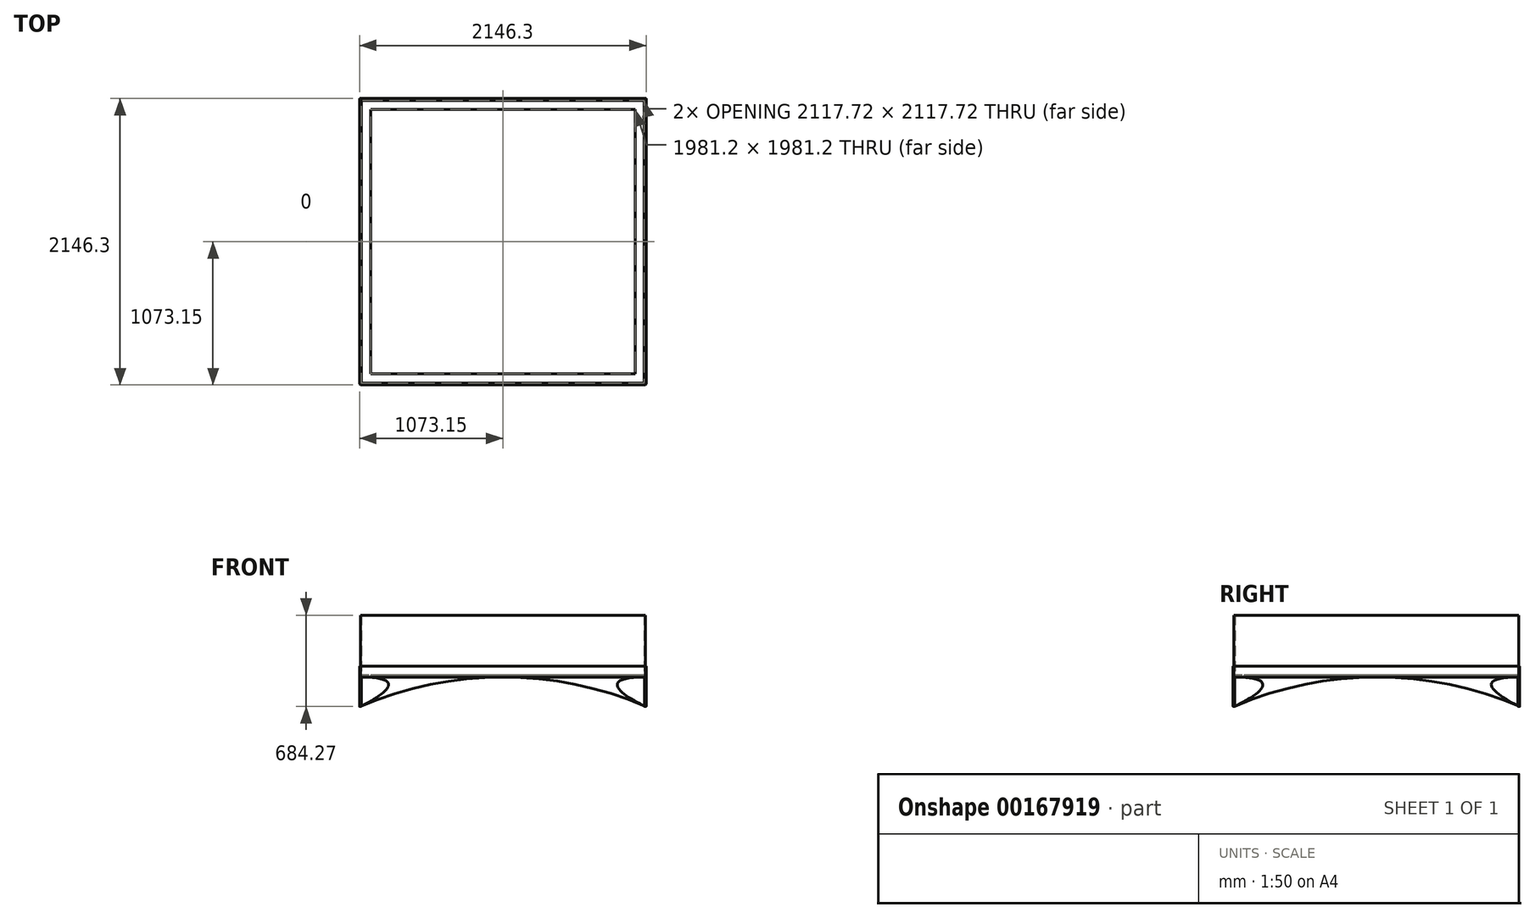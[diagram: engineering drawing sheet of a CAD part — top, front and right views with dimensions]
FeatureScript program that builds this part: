
annotation { "Feature Type Name" : "Feature", "Feature Type Description" : "" }
export const myFeature = defineFeature(function(context is Context, id is Id, definition is map)
    precondition{}
    {
        {
            var Q0;
            Q0=qCreatedBy(makeId("Top.planeOp"),FACE);
            var sketch = newSketch(context, id + "F0", { "sketchPlane" : qUnion([Q0])});
            skLineSegment(sketch, "E0.bottom", {"start": v(1066.8, 1066.8) * mm, "end": v(-1060.45, 1066.8) * mm});
            skLineSegment(sketch, "E0.top", {"start": v(1066.8, -1066.8) * mm, "end": v(-1066.8, -1066.8) * mm});
            skLineSegment(sketch, "E0.left", {"start": v(1066.8, 1066.8) * mm, "end": v(1066.8, -1066.8) * mm});
            skLineSegment(sketch, "E0.right", {"start": v(-1066.8, 1060.45) * mm, "end": v(-1066.8, -1066.8) * mm});
            skPoint(sketch, "E0.middle", {"position": v(0, 0) * mm});
            skLineSegment(sketch, "E1", {"start": v(-1073.15, 1066.8) * mm, "end": v(-1073.15, -1066.8) * mm});
            skLineSegment(sketch, "E2", {"start": v(-1066.8, 1073.15) * mm, "end": v(1066.8, 1073.15) * mm});
            skLineSegment(sketch, "E3", {"start": v(-1066.8, 1073.15) * mm, "end": v(-1073.15, 1066.8) * mm});
            skLineSegment(sketch, "E4.MirrorCS", {"start": v(1073.15, 1066.8) * mm, "end": v(1073.15, -1066.8) * mm});
            skLineSegment(sketch, "E5.MirrorCS", {"start": v(1066.8, 1073.15) * mm, "end": v(1073.15, 1066.8) * mm});
            skLineSegment(sketch, "E6.MirrorCS", {"start": v(-1066.8, -1073.15) * mm, "end": v(1066.8, -1073.15) * mm});
            skLineSegment(sketch, "E7.MirrorCS", {"start": v(1066.8, -1073.15) * mm, "end": v(1073.15, -1066.8) * mm});
            skLineSegment(sketch, "E8.MirrorCS", {"start": v(1066.8, -1066.8) * mm, "end": v(1066.8, 1066.8) * mm});
            skLineSegment(sketch, "E9.MirrorCS", {"start": v(1073.15, -1066.8) * mm, "end": v(1073.15, 1066.8) * mm});
            skLineSegment(sketch, "E10.MirrorCS", {"start": v(-1066.8, -1073.15) * mm, "end": v(-1073.15, -1066.8) * mm});
            skLineSegment(sketch, "E11.bottom", {"start": v(990.6, 990.6) * mm, "end": v(-990.6, 990.6) * mm});
            skLineSegment(sketch, "E11.top", {"start": v(990.6, -990.6) * mm, "end": v(-990.6, -990.6) * mm});
            skLineSegment(sketch, "E11.left", {"start": v(990.6, 990.6) * mm, "end": v(990.6, -990.6) * mm});
            skLineSegment(sketch, "E11.right", {"start": v(-990.6, 990.6) * mm, "end": v(-990.6, -990.6) * mm});
            skLineSegment(sketch, "E12.bottom", {"start": v(1052.51, 1058.86) * mm, "end": v(-1052.51, 1058.86) * mm});
            skLineSegment(sketch, "E12.top", {"start": v(1058.86, -1058.86) * mm, "end": v(-1058.86, -1058.86) * mm});
            skLineSegment(sketch, "E12.left", {"start": v(1058.86, 1052.51) * mm, "end": v(1058.86, -1058.86) * mm});
            skLineSegment(sketch, "E12.right", {"start": v(-1058.86, 1052.51) * mm, "end": v(-1058.86, -1058.86) * mm});
            skPoint(sketch, "E13.visualSharp", {"position": v(-1058.86, 1058.86) * mm});
            skArc(sketch, "E13.filletArc", {"start": v(-1052.51, 1058.86) * mm, "mid": v(-1057, 1057) * mm, "end": v(-1058.86, 1052.51) * mm});
            skPoint(sketch, "E14.visualSharp", {"position": v(-1066.8, 1066.8) * mm});
            skArc(sketch, "E14.filletArc", {"start": v(-1060.45, 1066.8) * mm, "mid": v(-1064.94, 1064.94) * mm, "end": v(-1066.8, 1060.45) * mm});
            skPoint(sketch, "E15.visualSharp", {"position": v(1058.86, 1058.86) * mm});
            skArc(sketch, "E15.filletArc", {"start": v(1058.86, 1052.51) * mm, "mid": v(1057, 1057) * mm, "end": v(1052.51, 1058.86) * mm});
            skSolve(sketch);
        }
        {
            var Q0;
            Q0 = qSketchRegion(id + "F0", true);
            extrude(context, id + "F1", {"entities" : qUnion([Q0]), "depth" : 76.2 * mm, "hasSecondDirection" : true, "secondDirectionOppositeDirection" : true, "secondDirectionDepth" : 6.35 * mm});
        }
        {
            var Q0;
            Q0=makeQuery(id+"F0.imprint","IMPRINT",FACE,{"disambiguationData":[TD([[makeQuery(id+"F0.imprint","IMPRINT",EDGE,{"derivedFrom":sQuery(id+"F0.wireOp",EDGE,"E0.bottom")}),1.0]])]});
            var Q1;
            Q1=makeQuery(id+"F0.imprint","IMPRINT",FACE,{"disambiguationData":[TD([[makeQuery(id+"F0.imprint","IMPRINT",EDGE,{"derivedFrom":sQuery(id+"F0.wireOp",EDGE,"E11.bottom")}),-1.0]])]});
            extrude(context, id + "F2", {"entities" : qUnion([Q0, Q1]), "operationType" : NewBodyOperationType.ADD, "oppositeDirection" : true, "depth" : 6.35 * mm});
        }
        {
            var Q0;
            Q0=makeQuery(id+"F0.imprint","IMPRINT",FACE,{"disambiguationData":[TD([[makeQuery(id+"F0.imprint","IMPRINT",EDGE,{"derivedFrom":sQuery(id+"F0.wireOp",EDGE,"E11.bottom")}),1.0]])]});
            var Q1;
            Q1=makeQuery(id+"F0.imprint","IMPRINT",FACE,{"disambiguationData":[TD([[makeQuery(id+"F0.imprint","IMPRINT",EDGE,{"derivedFrom":sQuery(id+"F0.wireOp",EDGE,"E0.bottom")}),1.0]])]});
            extrude(context, id + "F3", {"entities" : qUnion([Q0, Q1]), "depth" : 9.52 * mm});
        }
        {
            var Q0;
            Q0=makeQuery(id+"F0.imprint","IMPRINT",FACE,{"disambiguationData":[TD([[makeQuery(id+"F0.imprint","IMPRINT",EDGE,{"derivedFrom":sQuery(id+"F0.wireOp",EDGE,"E0.bottom")}),1.0]])]});
            extrude(context, id + "F4", {"entities" : qUnion([Q0]), "depth" : 457.2 * mm});
        }
        {
            var Q0;
            Q0=makeQuery(id+"F1.opExtrude","SWEPT_FACE",FACE,{"disambiguationData":[OSD([sQuery(id+"F0.wireOp",EDGE,"E6.MirrorCS")])]});
            var sketch = newSketch(context, id + "F5", { "sketchPlane" : qUnion([Q0])});
            skArc(sketch, "E16", {"start": v(1066.8, -224.76) * mm, "mid": v(-0.24, -6.61) * mm, "end": v(-1066.8, -227.07) * mm});
            skPoint(sketch, "E16.endSnap0", {"position": v(-1066.8, 34.93) * mm});
            skFitSpline(sketch, "E17", {"points": [v(-1066.8, -6.35) * mm, v(-1066.8, -227.07) * mm], "startDerivative": vector(1189.41, 0) * mm, "endDerivative": vector(-424.25, -208.28) * mm});
            skFitSpline(sketch, "E18", {"points": [v(1066.8, -6.35) * mm, v(1066.8, -224.76) * mm], "startDerivative": vector(-1161.94, 0) * mm, "endDerivative": vector(443.87, -209.2) * mm});
            skSolve(sketch);
        }
        {
            var Q0;
            Q0=makeQuery(id+"F5.imprint","IMPRINT",FACE,{"disambiguationData":[TD([[makeQuery(id+"F5.imprint","IMPRINT",EDGE,{"derivedFrom":sQuery(id+"F5.wireOp",EDGE,"E16")}),-1.0]])]});
            extrude(context, id + "F6", {"entities" : qUnion([Q0]), "oppositeDirection" : true, "depth" : 12.7 * mm});
        }
        {
            var Q0;
            Q0=makeQuery(id+"F6.opExtrude","SWEPT_BODY",BODY,{"disambiguationData":[OSD([sQuery(id+"F0.wireOp",EDGE,"E6.MirrorCS"),sQuery(id+"F5.wireOp",EDGE,"E16"),sQuery(id+"F5.wireOp",EDGE,"E17"),sQuery(id+"F5.wireOp",EDGE,"E18")])]});
            transform(context, id + "F7", {"entities" : qUnion([Q0]), "transformType" : TransformType.TRANSLATION_3D, "dx" : 0 * mm, "dy" : 2133.6 * mm, "dz" : 0 * mm, "makeCopy" : true});
        }
        {
            var Q0;
            Q0=makeQuery(id+"F7.opPattern","COPY",BODY,{"derivedFrom":makeQuery(id+"F6.opExtrude","SWEPT_BODY",BODY,{"disambiguationData":[OSD([sQuery(id+"F0.wireOp",EDGE,"E6.MirrorCS"),sQuery(id+"F5.wireOp",EDGE,"E16"),sQuery(id+"F5.wireOp",EDGE,"E17"),sQuery(id+"F5.wireOp",EDGE,"E18")])]}),"instanceName":"1"});
            var Q1;
            Q1=makeQuery(id+"F1.opExtrude","SWEPT_EDGE",EDGE,{"disambiguationData":[OSD([sQuery(id+"F0.wireOp",EDGE,"E2"),sQuery(id+"F0.wireOp",EDGE,"E3")])]});
            transform(context, id + "F8", {"entities" : qUnion([Q0]), "transformType" : TransformType.ROTATION, "transformAxis" : qUnion([Q1]), "angle" : 90 * degree, "makeCopy" : true});
        }
        {
            var Q0;
            Q0=makeQuery(id+"F8.opPattern","COPY",BODY,{"derivedFrom":makeQuery(id+"F7.opPattern","COPY",BODY,{"derivedFrom":makeQuery(id+"F6.opExtrude","SWEPT_BODY",BODY,{"disambiguationData":[OSD([sQuery(id+"F0.wireOp",EDGE,"E6.MirrorCS"),sQuery(id+"F5.wireOp",EDGE,"E16"),sQuery(id+"F5.wireOp",EDGE,"E17"),sQuery(id+"F5.wireOp",EDGE,"E18")])]}),"instanceName":"1"}),"instanceName":"1"});
            var Q1;
            Q1=makeQuery(id+"F1.opExtrude","CAP_EDGE",EDGE,{"disambiguationData":[OSD([sQuery(id+"F0.wireOp",EDGE,"E2")])],"isStart":true});
            transform(context, id + "F9", {"entities" : qUnion([Q0]), "transformType" : TransformType.TRANSLATION_DISTANCE, "transformDirection" : qUnion([Q1]), "distance" : 6.35 * mm, "makeCopy" : false});
        }
        {
            var Q0;
            Q0=makeQuery(id+"F8.opPattern","COPY",BODY,{"derivedFrom":makeQuery(id+"F7.opPattern","COPY",BODY,{"derivedFrom":makeQuery(id+"F6.opExtrude","SWEPT_BODY",BODY,{"disambiguationData":[OSD([sQuery(id+"F0.wireOp",EDGE,"E6.MirrorCS"),sQuery(id+"F5.wireOp",EDGE,"E16"),sQuery(id+"F5.wireOp",EDGE,"E17"),sQuery(id+"F5.wireOp",EDGE,"E18")])]}),"instanceName":"1"}),"instanceName":"1"});
            transform(context, id + "F10", {"entities" : qUnion([Q0]), "transformType" : TransformType.TRANSLATION_3D, "dx" : 2133.6 * mm, "dy" : 0 * mm, "dz" : 0 * mm, "makeCopy" : true});
        }
    });
